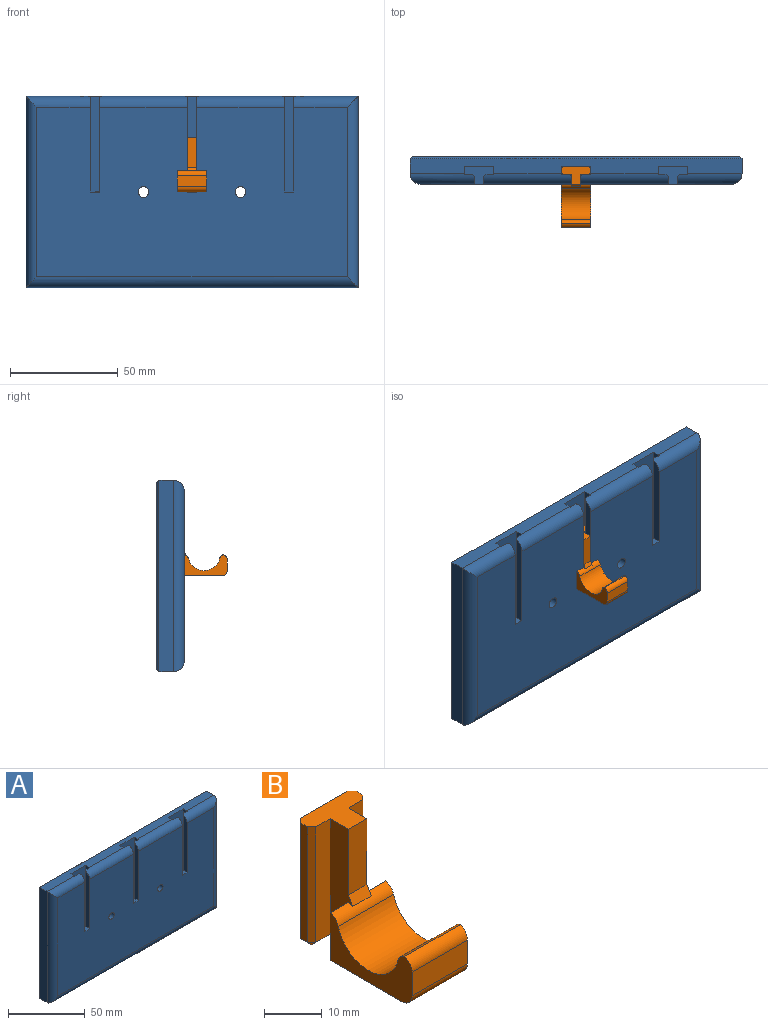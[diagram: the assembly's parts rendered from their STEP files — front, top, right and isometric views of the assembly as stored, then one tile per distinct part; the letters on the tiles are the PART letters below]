
ASSEMBLY  parts=2 mates=1
PART A: 49 faces, bbox 154x12.7x88.7 mm
  f0: plane 154x6.7mm, normal (0,0,1), area 902.2mm2, adj f2,f3,f4,f5,f7,f10,f13,f17
  f1: plane 144x78.68mm, normal (0,-1,0), area 10759.6mm2, adj f2,f3,f4,f13,f14,f15,f16,f20
  f2: cylinder r=5mm len=40.5mm, axis (1,0,0), area 312.6mm2, adj f0,f1,f18,f19,f20,f33,f38,f39
  f3: cylinder r=5mm len=29.75mm, axis (1,0,0), area 216.6mm2, adj f0,f1,f15,f25,f30,f31,f43
  f4: cylinder r=5mm len=40.5mm, axis (1,0,0), area 312.6mm2, adj f0,f1,f21,f22,f23,f27,f28,f29
  f5: plane 88.68x6.7mm, normal (-1,0,0), area 594.2mm2, adj f0,f6,f12,f14
  f6: plane 154x6.7mm, normal (0,0,-1), area 1031.8mm2, adj f5,f7,f11,f16
  f7: plane 88.68x6.7mm, normal (1,0,0), area 594.2mm2, adj f0,f6,f9,f15
  f8: plane 152x86.68mm, normal (0,1,0), area 13136.1mm2, adj f9,f10,f11,f12,f47,f48
  f9: plane 88.68x1mm, normal (0.71,0.71,0), area 124mm2, adj f7,f8,f10,f11
  f10: plane 154x1mm, normal (0,0.71,0.71), area 216.4mm2, adj f0,f8,f9,f12
  f11: plane 154x1mm, normal (0,0.71,-0.71), area 216.4mm2, adj f6,f8,f9,f12
  f12: plane 88.68x1mm, normal (-0.71,0.71,0), area 124mm2, adj f5,f8,f10,f11
  f13: cylinder r=5mm len=29.75mm, axis (1,0,0), area 216.6mm2, adj f0,f1,f14,f35,f36,f37,f41
  f14: cylinder r=5mm len=88.68mm, axis (0,0,1), area 668mm2, adj f1,f5,f13,f16
  f15: cylinder r=5mm len=88.68mm, axis (0,0,-1), area 668mm2, adj f1,f3,f7,f16
  f16: cylinder r=5mm len=154mm, axis (-1,0,0), area 1181mm2, adj f1,f6,f14,f15
  f17: plane 44.34x13.5mm, normal (0,-1,0), area 598.6mm2, adj f0,f18,f23,f24
  f18: plane 44.34x3.7mm, normal (1,0,0), area 164.1mm2, adj f0,f2,f17,f19,f24
  f19: plane 44.32x3.5mm, normal (0,1,0), area 155.1mm2, adj f2,f18,f24,f46
  f20: plane 44.11x3.5mm, normal (1,0,0), area 149.9mm2, adj f1,f2,f24,f46
  f21: plane 44.11x3.5mm, normal (-1,0,0), area 149.9mm2, adj f1,f4,f24,f45
  f22: plane 44.32x3.5mm, normal (0,1,0), area 155.1mm2, adj f4,f23,f24,f45
  f23: plane 44.34x3.7mm, normal (-1,0,0), area 164.1mm2, adj f0,f4,f17,f22,f24
  f24: plane 13.5x8.2mm, normal (0,0,1), area 71.2mm2, adj f1,f17,f18,f19,f20,f21,f22,f23
  f25: plane 44.34x3.7mm, normal (-1,0,0), area 164.1mm2, adj f0,f3,f26,f31,f32
  f26: plane 44.34x13.5mm, normal (0,-1,0), area 598.6mm2, adj f0,f25,f27,f32
  f27: plane 44.34x3.7mm, normal (1,0,0), area 164.1mm2, adj f0,f4,f26,f28,f32
  f28: plane 44.32x3.5mm, normal (0,1,0), area 155.1mm2, adj f4,f27,f32,f44
  f29: plane 44.11x3.5mm, normal (1,0,0), area 149.9mm2, adj f1,f4,f32,f44
  f30: plane 44.11x3.5mm, normal (-1,0,0), area 149.9mm2, adj f1,f3,f32,f43
  f31: plane 44.32x3.5mm, normal (0,1,0), area 155.1mm2, adj f3,f25,f32,f43
  f32: plane 13.5x8.2mm, normal (0,0,1), area 71.2mm2, adj f1,f25,f26,f27,f28,f29,f30,f31
  f33: plane 44.34x3.7mm, normal (-1,0,0), area 164.1mm2, adj f0,f2,f34,f39,f40
  f34: plane 44.34x13.5mm, normal (0,-1,0), area 598.6mm2, adj f0,f33,f35,f40
  f35: plane 44.34x3.7mm, normal (1,0,0), area 164.1mm2, adj f0,f13,f34,f36,f40
  f36: plane 44.32x3.5mm, normal (0,1,0), area 155.1mm2, adj f13,f35,f40,f41
  f37: plane 44.11x3.5mm, normal (1,0,0), area 149.9mm2, adj f1,f13,f40,f41
  f38: plane 44.11x3.5mm, normal (-1,0,0), area 149.9mm2, adj f1,f2,f40,f42
  f39: plane 44.32x3.5mm, normal (0,1,0), area 155.1mm2, adj f2,f33,f40,f42
  f40: plane 13.5x8.2mm, normal (0,0,1), area 71.2mm2, adj f1,f33,f34,f35,f36,f37,f38,f39
  f41: plane 44.33x1.01mm, normal (0.71,0.71,0), area 62.6mm2, adj f13,f36,f37,f40
  f42: plane 44.33x1.01mm, normal (-0.71,0.71,0), area 62.6mm2, adj f2,f38,f39,f40
  f43: plane 44.33x1.01mm, normal (-0.71,0.71,0), area 62.6mm2, adj f3,f30,f31,f32
  f44: plane 44.33x1.01mm, normal (0.71,0.71,0), area 62.6mm2, adj f4,f28,f29,f32
  f45: plane 44.33x1.01mm, normal (-0.71,0.71,0), area 62.6mm2, adj f4,f21,f22,f24
  f46: plane 44.33x1.01mm, normal (0.71,0.71,0), area 62.6mm2, adj f2,f19,f20,f24
  f47: cylinder r=2.5mm len=12.7mm, axis (0,-1,0), area 199.5mm2, adj f1,f8
  f48: cylinder r=2.5mm len=12.7mm, axis (0,-1,0), area 199.5mm2, adj f1,f8
PART B: 36 faces, bbox 13.5x28.2x25.4 mm
  f0: plane 13.87x4.5mm, normal (0,-1,0), area 62.4mm2, adj f4,f5,f8,f20
  f1: plane 24.4x11.5mm, normal (0,1,0), area 280.6mm2, adj f8,f25,f28,f29
  f2: plane 24.4x1.7mm, normal (-1,0,0), area 41.5mm2, adj f8,f22,f25,f26
  f3: plane 24.4x3.5mm, normal (0,-1,0), area 85.4mm2, adj f4,f8,f22,f23
  f4: plane 24.4x5.51mm, normal (-1,0,0), area 110.5mm2, adj f0,f3,f8,f11,f16,f20,f21
  f5: plane 24.4x5.51mm, normal (1,0,0), area 110.5mm2, adj f0,f6,f8,f10,f16,f20,f35
  f6: plane 24.4x3.5mm, normal (0,-1,0), area 85.4mm2, adj f5,f8,f31,f34
  f7: plane 24.4x1.7mm, normal (1,0,0), area 41.5mm2, adj f8,f28,f31,f32
  f8: plane 13.5x8.2mm, normal (0,0,1), area 68.2mm2, adj f0,f1,f2,f3,f4,f5,f6,f7
  f9: plane 24.7x13.5mm, normal (0,0,-1), area 269.6mm2, adj f10,f11,f14,f15,f19,f21,f23,f26
  f10: plane 10x5.5mm, normal (0,1,0), area 45.5mm2, adj f5,f9,f14,f16,f35
  f11: plane 10x5.5mm, normal (0,1,0), area 45.5mm2, adj f4,f9,f15,f16,f21
  f12: cylinder r=7.5mm len=14.53mm, axis (-1,0,0), area 267.3mm2, adj f14,f15,f16,f18
  f13: plane 13.5x5mm, normal (0,-1,0), area 67.5mm2, adj f14,f15,f17,f19
  f14: plane 20x10mm, normal (1,0,0), area 107.3mm2, adj f9,f10,f12,f13,f16,f17,f18,f19
  f15: plane 20x10mm, normal (-1,0,0), area 107.3mm2, adj f9,f11,f12,f13,f16,f17,f18,f19
  f16: cylinder r=2.5mm len=13.5mm, axis (-1,0,0), area 33.9mm2, adj f4,f5,f10,f11,f12,f14,f15,f20
  f17: cylinder r=2.5mm len=13.5mm, axis (1,0,0), area 43.1mm2, adj f13,f14,f15,f18
  f18: cylinder r=2.5mm len=13.5mm, axis (-1,0,0), area 34.5mm2, adj f12,f14,f15,f17
  f19: cylinder r=2.5mm len=13.5mm, axis (1,0,0), area 53mm2, adj f9,f13,f14,f15
  f20: plane 4.5x1.94mm, normal (0,-0.89,0.46), area 9.9mm2, adj f0,f4,f5,f16
  f21: plane 5.5x1mm, normal (-0.71,0,-0.71), area 7.1mm2, adj f4,f9,f11,f23
  f22: plane 24.4x1mm, normal (-0.71,-0.71,0), area 34.5mm2, adj f2,f3,f8,f24
  f23: plane 4.5x1mm, normal (0,-0.71,-0.71), area 5.7mm2, adj f3,f9,f21,f24
  f24: plane 1x1mm, normal (-0.58,-0.58,-0.58), area 0.9mm2, adj f22,f23,f26
  f25: plane 24.4x1mm, normal (-0.71,0.71,0), area 34.5mm2, adj f1,f2,f8,f27
  f26: plane 1.7x1mm, normal (-0.71,0,-0.71), area 2.4mm2, adj f2,f9,f24,f27
  f27: plane 1x1mm, normal (-0.58,0.58,-0.58), area 0.9mm2, adj f25,f26,f29
  f28: plane 24.4x1mm, normal (0.71,0.71,0), area 34.5mm2, adj f1,f7,f8,f30
  f29: plane 11.5x1mm, normal (0,0.71,-0.71), area 16.3mm2, adj f1,f9,f27,f30
  f30: plane 1x1mm, normal (0.58,0.58,-0.58), area 0.9mm2, adj f28,f29,f32
  f31: plane 24.4x1mm, normal (0.71,-0.71,0), area 34.5mm2, adj f6,f7,f8,f33
  f32: plane 1.7x1mm, normal (0.71,0,-0.71), area 2.4mm2, adj f7,f9,f30,f33
  f33: plane 1x1mm, normal (0.58,-0.58,-0.58), area 0.9mm2, adj f31,f32,f34
  f34: plane 4.5x1mm, normal (0,-0.71,-0.71), area 5.7mm2, adj f6,f9,f33,f35
  f35: plane 5.5x1mm, normal (0.71,0,-0.71), area 7.1mm2, adj f5,f9,f10,f34
PLACE A t=(0,0,65.37)mm fixed
PLACE B t=(0,0.02,-8.97)mm
MATE slider A.f24 <-> B.f8  axis (0,0,1) through (0,-7.55,65.37)mm
